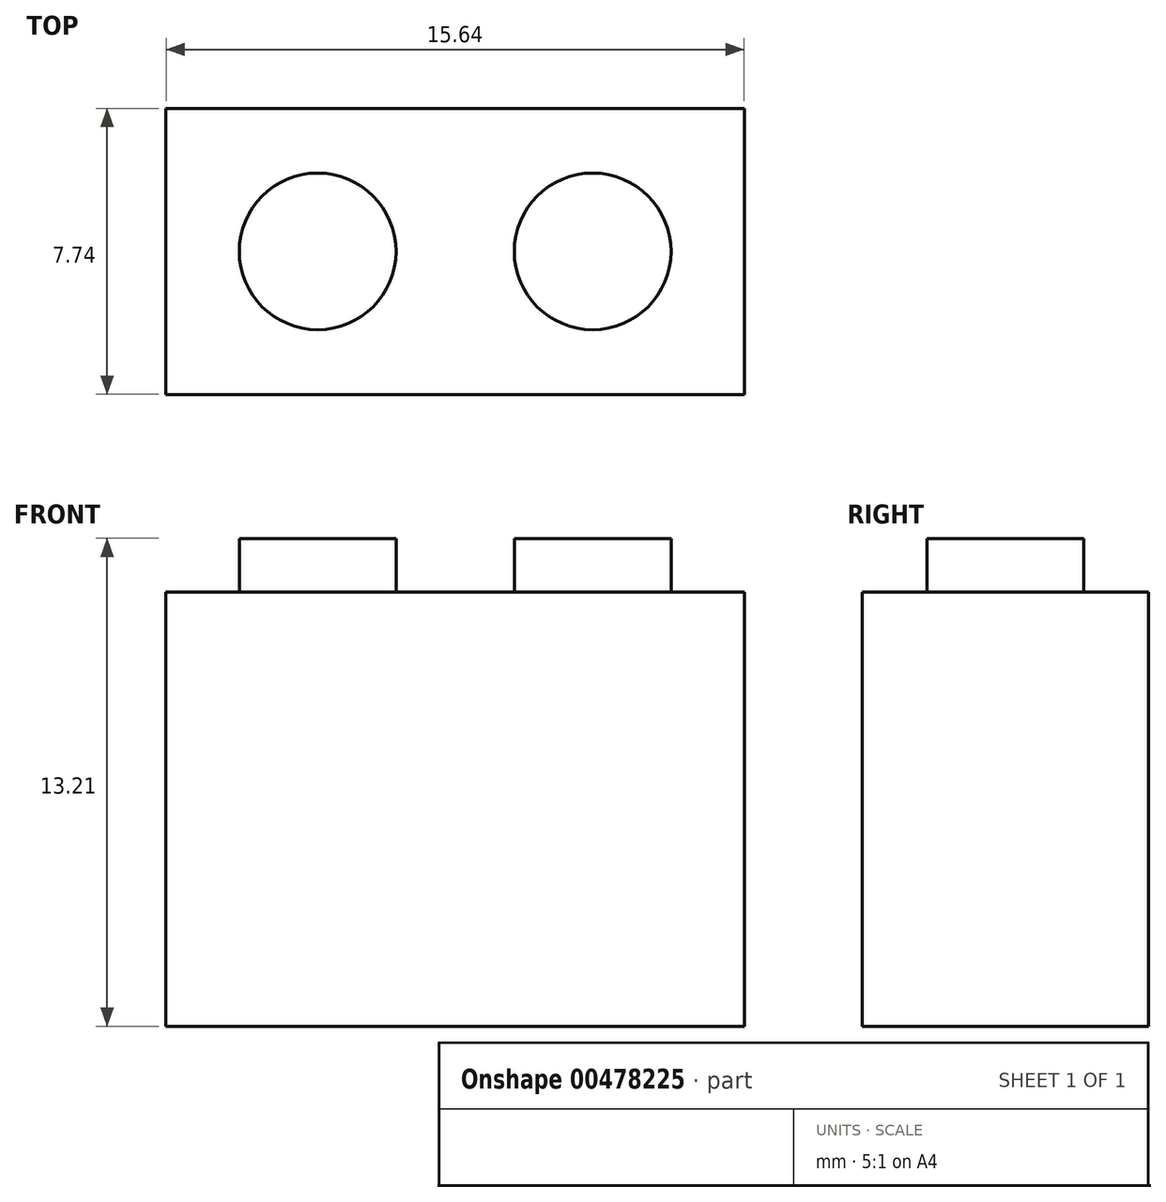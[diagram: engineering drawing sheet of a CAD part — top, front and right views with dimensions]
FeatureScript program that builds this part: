
annotation { "Feature Type Name" : "Feature", "Feature Type Description" : "" }
export const myFeature = defineFeature(function(context is Context, id is Id, definition is map)
    precondition{}
    {
        {
            var Q0;
            Q0=qCreatedBy(makeId("Top.planeOp"),FACE);
            var sketch = newSketch(context, id + "F0", { "sketchPlane" : qUnion([Q0])});
            skLineSegment(sketch, "E0.bottom", {"start": v(-7.82, 3.87) * mm, "end": v(7.82, 3.87) * mm});
            skLineSegment(sketch, "E0.top", {"start": v(-7.82, -3.87) * mm, "end": v(7.82, -3.87) * mm});
            skLineSegment(sketch, "E0.left", {"start": v(-7.82, 3.87) * mm, "end": v(-7.82, -3.87) * mm});
            skLineSegment(sketch, "E0.right", {"start": v(7.82, 3.87) * mm, "end": v(7.82, -3.87) * mm});
            skPoint(sketch, "E0.middle", {"position": v(0, 0) * mm});
            skSolve(sketch);
        }
        {
            var Q0;
            Q0=makeQuery(id+"F0.imprint","IMPRINT",FACE,{"disambiguationData":[TD([[makeQuery(id+"F0.imprint","IMPRINT",EDGE,{"derivedFrom":sQuery(id+"F0.wireOp",EDGE,"E0.bottom")}),-1.0]])]});
            extrude(context, id + "F1", {"entities" : qUnion([Q0]), "depth" : 9.4 * mm});
        }
        {
            var Q0;
            Q0=makeQuery(id+"F1.opExtrude","CAP_FACE",FACE,{"disambiguationData":[OSD([sQuery(id+"F0.wireOp",EDGE,"E0.bottom"),sQuery(id+"F0.wireOp",EDGE,"E0.top"),sQuery(id+"F0.wireOp",EDGE,"E0.left"),sQuery(id+"F0.wireOp",EDGE,"E0.right")])],"isStart":false});
            var sketch = newSketch(context, id + "F2", { "sketchPlane" : qUnion([Q0])});
            skCircle(sketch, "E1", {"center": v(-3.72, 0) * mm, "radius": 2.12 * mm});
            skCircle(sketch, "E2.MirrorC", {"center": v(3.72, 0) * mm, "radius": 2.12 * mm});
            skSolve(sketch);
        }
        {
            var Q0;
            Q0=makeQuery(id+"F2.imprint","IMPRINT",FACE,{"disambiguationData":[TD([[makeQuery(id+"F2.imprint","IMPRINT",EDGE,{"derivedFrom":sQuery(id+"F2.wireOp",EDGE,"E1")}),-1.0]])]});
            extrude(context, id + "F3", {"entities" : qUnion([Q0]), "operationType" : NewBodyOperationType.ADD, "depth" : 2.36 * mm});
        }
        {
            var Q0;
            Q0=makeQuery(id+"F3.boolean.opBoolean","SPLIT",FACE,{"disambiguationData":[TD([makeQuery(id+"F3.opExtrude","SWEPT_FACE",FACE,{"disambiguationData":[OSD([sQuery(id+"F2.wireOp",EDGE,"E2.MirrorC")])]})])],"derivedFrom":makeQuery(id+"F1.opExtrude","CAP_FACE",FACE,{"disambiguationData":[OSD([sQuery(id+"F0.wireOp",EDGE,"E0.bottom"),sQuery(id+"F0.wireOp",EDGE,"E0.top"),sQuery(id+"F0.wireOp",EDGE,"E0.left"),sQuery(id+"F0.wireOp",EDGE,"E0.right")])],"isStart":false})});
            var Q1;
            Q1=makeQuery(id+"F3.boolean.opBoolean","SPLIT",FACE,{"disambiguationData":[TD([makeQuery(id+"F3.opExtrude","SWEPT_FACE",FACE,{"disambiguationData":[OSD([sQuery(id+"F2.wireOp",EDGE,"E1")])]})])],"derivedFrom":makeQuery(id+"F1.opExtrude","CAP_FACE",FACE,{"disambiguationData":[OSD([sQuery(id+"F0.wireOp",EDGE,"E0.bottom"),sQuery(id+"F0.wireOp",EDGE,"E0.top"),sQuery(id+"F0.wireOp",EDGE,"E0.left"),sQuery(id+"F0.wireOp",EDGE,"E0.right")])],"isStart":false})});
            extrude(context, id + "F4", {"entities" : qUnion([Q0, Q1]), "operationType" : NewBodyOperationType.ADD, "depth" : 1.73 * mm});
        }
        {
            var Q0;
            {var subQ0=sQuery(id+"F0.wireOp",EDGE,"E0.right");var subQ1=sQuery(id+"F0.wireOp",EDGE,"E0.left");var subQ2=sQuery(id+"F0.wireOp",EDGE,"E0.top");var subQ3=sQuery(id+"F0.wireOp",EDGE,"E0.bottom");Q0=makeQuery(id+"F4.opExtrude","CAP_FACE",FACE,{"disambiguationData":[OSD([subQ3,subQ2,subQ1,subQ0]),TDD([makeQuery(id+"F3.boolean.opBoolean","SPLIT",FACE,{"disambiguationData":[TD([makeQuery(id+"F3.opExtrude","SWEPT_FACE",FACE,{"disambiguationData":[OSD([sQuery(id+"F2.wireOp",EDGE,"E1")])]})])],"derivedFrom":makeQuery(id+"F1.opExtrude","CAP_FACE",FACE,{"disambiguationData":[OSD([subQ3,subQ2,subQ1,subQ0])],"isStart":false})})])],"isStart":false});}
            var Q1;
            {var subQ0=sQuery(id+"F0.wireOp",EDGE,"E0.right");var subQ1=sQuery(id+"F0.wireOp",EDGE,"E0.left");var subQ2=sQuery(id+"F0.wireOp",EDGE,"E0.top");var subQ3=sQuery(id+"F0.wireOp",EDGE,"E0.bottom");Q1=makeQuery(id+"F4.opExtrude","CAP_FACE",FACE,{"disambiguationData":[OSD([subQ3,subQ2,subQ1,subQ0]),TDD([makeQuery(id+"F3.boolean.opBoolean","SPLIT",FACE,{"disambiguationData":[TD([makeQuery(id+"F3.opExtrude","SWEPT_FACE",FACE,{"disambiguationData":[OSD([sQuery(id+"F2.wireOp",EDGE,"E2.MirrorC")])]})])],"derivedFrom":makeQuery(id+"F1.opExtrude","CAP_FACE",FACE,{"disambiguationData":[OSD([subQ3,subQ2,subQ1,subQ0])],"isStart":false})})])],"isStart":false});}
            extrude(context, id + "F5", {"entities" : qUnion([Q0, Q1]), "operationType" : NewBodyOperationType.ADD, "depth" : 2.08 * mm});
        }
    });
